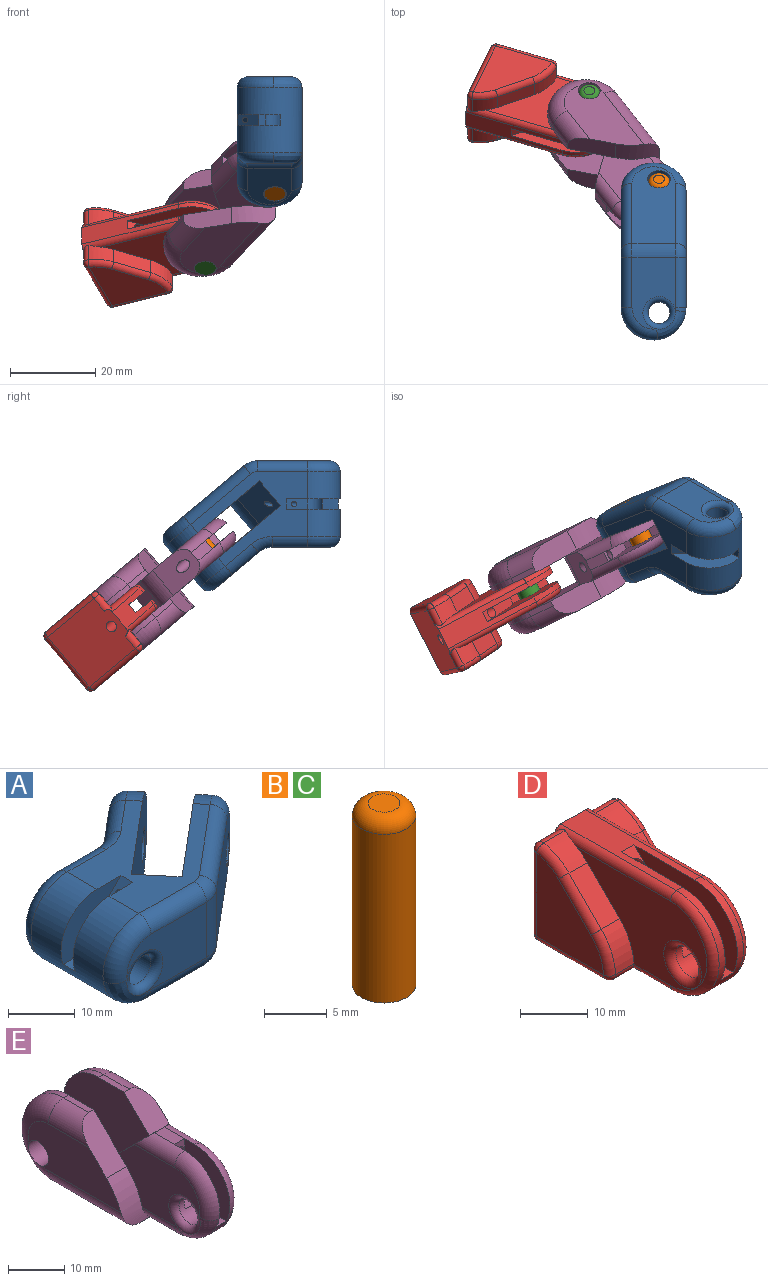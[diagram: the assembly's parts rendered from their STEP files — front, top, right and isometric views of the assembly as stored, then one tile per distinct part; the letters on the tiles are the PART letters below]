
ASSEMBLY  parts=5 mates=6
PART A: 47 faces, bbox 43.2x31.9x17 mm
  f0: cylinder r=7.62mm len=15.24mm, axis (0,1,0), area 327.8mm2, adj f9,f10,f21,f22,f23,f31,f32,f33
  f1: cylinder r=2.54mm len=17.78mm, axis (0,-1,0), area 266.9mm2, adj f17,f18,f41,f42,f43,f44
  f2: plane 20.43x17.14mm, normal (-0.64,0.77,0), area 264.5mm2, adj f3,f9,f10,f12,f13,f14,f15
  f3: plane 5.84x4.9mm, normal (0.77,0.64,0), area 24.3mm2, adj f2,f4,f10,f14
  f4: plane 20.43x17.14mm, normal (0.64,-0.77,0), area 264.5mm2, adj f3,f9,f10,f11,f13,f14,f16
  f5: plane 10.16x10.06mm, normal (-0.64,0.77,0), area 100mm2, adj f16,f19,f38,f39,f40
  f6: plane 13.39x10.16mm, normal (0,1,0), area 81.8mm2, adj f17,f19,f32,f33,f34,f35
  f7: plane 16.84x10.16mm, normal (0,-1,0), area 116.8mm2, adj f18,f20,f22,f23,f24,f25
  f8: plane 18.04x15.14mm, normal (0.64,-0.77,0), area 205.9mm2, adj f15,f20,f28,f29,f30
  f9: plane 27.54x22.2mm, normal (0,0,1), area 215.7mm2, adj f0,f2,f4,f11,f12,f13,f25,f27
  f10: plane 27.54x22.2mm, normal (0,0,-1), area 296.3mm2, adj f0,f2,f3,f4,f11,f12,f24,f26
  f11: cylinder r=7.62mm len=15.24mm, axis (0.64,-0.77,0), area 60.8mm2, adj f4,f9,f10,f40
  f12: cylinder r=7.62mm len=15.24mm, axis (0.64,-0.77,0), area 60.8mm2, adj f2,f9,f10,f30
  f13: plane 10.65x10.53mm, normal (0.54,0.45,0.71), area 69.4mm2, adj f2,f4,f9,f14,f45
  f14: cylinder r=7.62mm len=7.27mm, axis (-0.64,0.77,0), area 45.6mm2, adj f2,f3,f4,f13
  f15: cylinder r=2.67mm len=7.35mm, axis (0.64,-0.77,0), area 85.1mm2, adj f2,f8
  f16: cylinder r=2.67mm len=7.35mm, axis (0.64,-0.77,0), area 85.1mm2, adj f4,f5
  f17: torus R=3.81mm, axis (0,-1,0), area 37.6mm2, adj f1,f6,f31
  f18: torus R=3.81mm, axis (0,-1,0), area 37.6mm2, adj f1,f7,f21
  f19: cylinder r=5.08mm len=10.16mm, axis (0,0,-1), area 36mm2, adj f5,f6,f36,f37
  f20: cylinder r=5.08mm len=10.16mm, axis (0,0,-1), area 36mm2, adj f7,f8,f26,f27
  f21: bspline ~6.87x6.87mm, area 32.4mm2, adj f0,f18,f22,f23
  f22: torus R=5.08mm, axis (0,-1,0), area 3.6mm2, adj f0,f7,f21,f24
  f23: torus R=5.08mm, axis (0,-1,0), area 45.6mm2, adj f0,f7,f21,f25
  f24: cylinder r=2.54mm len=11.76mm, axis (1,0,0), area 46.9mm2, adj f7,f10,f22,f26
  f25: cylinder r=2.54mm len=11.76mm, axis (-1,0,0), area 46.9mm2, adj f7,f9,f23,f27
  f26: torus R=2.54mm, axis (0,0,1), area 11.6mm2, adj f10,f20,f24,f28
  f27: torus R=2.54mm, axis (0,0,1), area 11.6mm2, adj f9,f20,f25,f29
  f28: cylinder r=2.54mm len=15.78mm, axis (0.77,0.64,0), area 73.7mm2, adj f8,f10,f26,f30
  f29: cylinder r=2.54mm len=15.78mm, axis (-0.77,-0.64,0), area 73.7mm2, adj f8,f9,f27,f30
  f30: torus R=5.08mm, axis (0.64,-0.77,0), area 83.9mm2, adj f8,f12,f28,f29
  f31: bspline ~6.87x6.87mm, area 32.4mm2, adj f0,f17,f32,f33
  f32: torus R=5.08mm, axis (0,-1,0), area 45.6mm2, adj f0,f6,f31,f34
  f33: torus R=5.08mm, axis (0,-1,0), area 3.6mm2, adj f0,f6,f31,f35
  f34: cylinder r=2.54mm len=8.31mm, axis (1,0,0), area 33.2mm2, adj f6,f9,f32,f36
  f35: cylinder r=2.54mm len=8.31mm, axis (-1,0,0), area 33.2mm2, adj f6,f10,f33,f37
  f36: torus R=7.62mm, axis (0,0,1), area 16.7mm2, adj f9,f19,f34,f38
  f37: torus R=7.62mm, axis (0,0,1), area 16.7mm2, adj f10,f19,f35,f39
  f38: cylinder r=2.54mm len=7.8mm, axis (0.77,0.64,0), area 32.1mm2, adj f5,f9,f36,f40
  f39: cylinder r=2.54mm len=7.8mm, axis (-0.77,-0.64,0), area 32.1mm2, adj f5,f10,f37,f40
  f40: torus R=5.08mm, axis (-0.64,0.77,0), area 83.9mm2, adj f5,f11,f38,f39
  f41: plane 12.7x10.16mm, normal (0,1,0), area 64.6mm2, adj f0,f1,f9,f42,f44,f46
  f42: plane 2.54x1.61mm, normal (-1,0,0), area 4.1mm2, adj f1,f41,f43,f46
  f43: plane 12.7x10.16mm, normal (0,-1,0), area 64.6mm2, adj f0,f1,f9,f42,f44,f46
  f44: plane 3.71x2.54mm, normal (0,0,1), area 9.4mm2, adj f0,f1,f41,f43
  f45: cylinder r=0.64mm len=7.67mm, axis (-1,0,0), area 24.3mm2, adj f13,f46
  f46: plane 5.08x5.08mm, normal (-0.71,0,0.71), area 16.5mm2, adj f9,f41,f42,f43,f45
PART B: 4 faces, bbox 5.5x5.5x17.8 mm
  f0: cylinder r=2.54mm len=16.51mm, axis (0,0,-1), area 263.5mm2, adj f2,f3
  f1: plane 2.54x2.54mm, normal (0,0,1), area 5.1mm2, adj f3
  f2: plane 5.08x5.08mm, normal (0,0,-1), area 20.3mm2, adj f0
  f3: torus R=1.27mm, axis (0,0,1), area 26.1mm2, adj f0,f1
PART C: same geometry as B
PART D: 52 faces, bbox 17.8x33.8x19.2 mm
  f0: plane 7.62x7.62mm, normal (0,-0.71,0.71), area 23.8mm2, adj f10,f11,f14,f16
  f1: plane 24.13x5.08mm, normal (0,0,1), area 90.3mm2, adj f3,f7,f10,f11,f15,f23,f26
  f2: cylinder r=2.67mm len=5.33mm, axis (1,0,0), area 57.1mm2, adj f10,f11,f12,f13,f50,f51
  f3: cylinder r=8.89mm len=17.78mm, axis (-1,0,0), area 96.4mm2, adj f1,f9,f10,f11,f12,f24,f27
  f4: plane 27.22x15.24mm, normal (-1,0,0), area 226.5mm2, adj f18,f19,f22,f23,f24,f25,f49,f50
  f5: plane 27.22x15.24mm, normal (1,0,0), area 226.5mm2, adj f17,f20,f21,f26,f27,f28,f42,f51
  f6: plane 15.09x13.96mm, normal (1,0,0), area 138.1mm2, adj f33,f35,f38,f39,f40
  f7: plane 16.51x15.24mm, normal (0,1,0), area 235mm2, adj f1,f16,f23,f26,f29,f32,f35,f36
  f8: plane 15.09x13.96mm, normal (-1,0,0), area 138.1mm2, adj f29,f30,f45,f46,f47
  f9: plane 22.86x15.24mm, normal (0,0,-1), area 258mm2, adj f3,f25,f28,f30,f32,f33,f42,f49
  f10: plane 21.59x12.7mm, normal (-1,0,0), area 161.1mm2, adj f0,f1,f2,f3,f12,f13,f14,f15
  f11: plane 21.59x12.7mm, normal (1,0,0), area 161.1mm2, adj f0,f1,f2,f3,f12,f13,f14,f15
  f12: plane 3.15x2.54mm, normal (0,0,1), area 8mm2, adj f2,f3,f10,f11
  f13: plane 2.73x2.54mm, normal (0,0,1), area 6.9mm2, adj f2,f10,f11,f14
  f14: plane 2.54x2.54mm, normal (0,-1,0), area 6.5mm2, adj f0,f10,f11,f13
  f15: plane 2.54x2.54mm, normal (0,-0.71,0.71), area 5.5mm2, adj f1,f10,f11,f16
  f16: cylinder r=1.27mm len=15.24mm, axis (0,1,0), area 111.5mm2, adj f0,f7,f15
  f17: plane 6.76x6.76mm, normal (0,-0.71,0.71), area 36.4mm2, adj f5,f20,f21,f39
  f18: plane 6.76x6.76mm, normal (0,-0.71,0.71), area 36.4mm2, adj f4,f19,f22,f46
  f19: cylinder r=10.16mm len=6.73mm, axis (1,0,0), area 28.7mm2, adj f4,f18,f47,f49
  f20: cylinder r=10.16mm len=6.73mm, axis (1,0,0), area 28.7mm2, adj f5,f17,f40,f42
  f21: cylinder r=10.16mm len=5.27mm, axis (-1,0,0), area 23.8mm2, adj f5,f17,f26,f36,f38
  f22: cylinder r=10.16mm len=5.27mm, axis (-1,0,0), area 23.8mm2, adj f4,f18,f23,f43,f45
  f23: cylinder r=1.27mm len=24.13mm, axis (0,1,0), area 44.5mm2, adj f1,f4,f7,f22,f24,f43
  f24: torus R=7.62mm, axis (1,0,0), area 52.8mm2, adj f3,f4,f23,f25
  f25: cylinder r=1.27mm len=8.9mm, axis (0,-1,0), area 16.1mm2, adj f4,f9,f24,f49
  f26: cylinder r=1.27mm len=24.13mm, axis (0,-1,0), area 44.5mm2, adj f1,f5,f7,f21,f27,f36
  f27: torus R=7.62mm, axis (1,0,0), area 52.8mm2, adj f3,f5,f26,f28
  f28: cylinder r=1.27mm len=8.9mm, axis (0,1,0), area 16.1mm2, adj f5,f9,f27,f42
  f29: cylinder r=1.27mm len=15.09mm, axis (0,0,-1), area 30.1mm2, adj f7,f8,f31,f44
  f30: cylinder r=1.27mm len=13.96mm, axis (0,-1,0), area 27.9mm2, adj f8,f9,f31,f48
  f31: sphere r=1.27mm, area 2.5mm2, adj f29,f30,f32
  f32: cylinder r=1.27mm len=15.24mm, axis (-1,0,0), area 30.4mm2, adj f7,f9,f31,f34
  f33: cylinder r=1.27mm len=13.96mm, axis (0,1,0), area 27.9mm2, adj f6,f9,f34,f41
  f34: sphere r=1.27mm, area 2.5mm2, adj f32,f33,f35
  f35: cylinder r=1.27mm len=15.09mm, axis (0,0,1), area 30.1mm2, adj f6,f7,f34,f37
  f36: cylinder r=1.27mm len=4.48mm, axis (-1,0,0), area 9.2mm2, adj f7,f21,f26,f37
  f37: sphere r=1.27mm, area 2.8mm2, adj f35,f36,f38
  f38: torus R=8.89mm, axis (-1,0,0), area 11.5mm2, adj f6,f21,f37,f39
  f39: cylinder r=1.27mm len=7.65mm, axis (0,0.71,0.71), area 19.1mm2, adj f6,f17,f38,f40
  f40: torus R=8.89mm, axis (-1,0,0), area 14.3mm2, adj f6,f20,f39,f41
  f41: sphere r=1.27mm, area 2.6mm2, adj f33,f40,f42
  f42: cylinder r=1.27mm len=5.08mm, axis (1,0,0), area 8.7mm2, adj f5,f9,f20,f28,f41
  f43: cylinder r=1.27mm len=4.48mm, axis (-1,0,0), area 9.2mm2, adj f7,f22,f23,f44
  f44: sphere r=1.27mm, area 2.8mm2, adj f29,f43,f45
  f45: torus R=8.89mm, axis (-1,0,0), area 11.5mm2, adj f8,f22,f44,f46
  f46: cylinder r=1.27mm len=7.65mm, axis (0,0.71,0.71), area 19.1mm2, adj f8,f18,f45,f47
  f47: torus R=8.89mm, axis (-1,0,0), area 14.3mm2, adj f8,f19,f46,f48
  f48: sphere r=1.27mm, area 2.6mm2, adj f30,f47,f49
  f49: cylinder r=1.27mm len=5.08mm, axis (1,0,0), area 8.7mm2, adj f4,f9,f19,f25,f48
  f50: torus R=3.94mm, axis (1,0,0), area 39.2mm2, adj f2,f4
  f51: torus R=3.94mm, axis (1,0,0), area 39.2mm2, adj f2,f5
PART E: 48 faces, bbox 18.8x47x20.3 mm
  f0: plane 8.29x8.29mm, normal (0,-0.71,0.71), area 55.2mm2, adj f2,f3,f12,f13,f27,f32
  f1: plane 21.59x17.78mm, normal (-1,0,0), area 284.6mm2, adj f4,f11,f14,f15,f18,f25,f28,f29
  f2: plane 20.32x12.7mm, normal (-1,0,0), area 159.1mm2, adj f0,f27,f28,f30,f38,f39,f41,f42
  f3: plane 6.35x1.27mm, normal (0,0,1), area 8.1mm2, adj f0,f12,f16,f32
  f4: plane 6.35x1.27mm, normal (0,0,1), area 8.1mm2, adj f1,f15,f25,f35
  f5: plane 5.08x2.54mm, normal (0,0,1), area 12.9mm2, adj f22,f28,f38,f47
  f6: cylinder r=2.67mm len=5.33mm, axis (1,0,0), area 57.1mm2, adj f19,f20,f21,f24,f30,f31
  f7: cylinder r=8.89mm len=8.03mm, axis (-1,0,0), area 25.5mm2, adj f14,f19,f40,f41,f44,f45
  f8: cylinder r=1.27mm len=8.89mm, axis (0,1,0), area 60.5mm2, adj f22,f23,f28
  f9: plane 20.32x12.7mm, normal (1,0,0), area 159.1mm2, adj f25,f26,f28,f31,f43,f44,f46,f47
  f10: plane 23.31x10.16mm, normal (1,0,0), area 174.6mm2, adj f18,f25,f26,f35,f36,f37
  f11: plane 7.62x6.26mm, normal (0,1,0), area 47.7mm2, adj f1,f12,f14,f29
  f12: plane 21.59x17.78mm, normal (1,0,0), area 284.6mm2, adj f0,f3,f11,f14,f16,f17,f28,f29
  f13: plane 23.31x10.16mm, normal (-1,0,0), area 174.6mm2, adj f0,f17,f27,f32,f33,f34
  f14: plane 26.67x10.16mm, normal (0,0,-1), area 135.5mm2, adj f1,f7,f11,f12,f15,f16,f26,f27
  f15: cylinder r=8.89mm len=17.78mm, axis (1,0,0), area 35.5mm2, adj f1,f4,f14,f36
  f16: cylinder r=8.89mm len=17.78mm, axis (1,0,0), area 35.5mm2, adj f3,f12,f14,f33
  f17: cylinder r=2.54mm len=5.08mm, axis (1,0,0), area 80.9mm2, adj f12,f13,f33
  f18: cylinder r=2.54mm len=5.08mm, axis (1,0,0), area 80.9mm2, adj f1,f10,f36
  f19: plane 3.15x2.54mm, normal (0,0,1), area 8mm2, adj f6,f7,f21,f24
  f20: plane 2.73x2.54mm, normal (0,0,1), area 6.9mm2, adj f6,f21,f23,f24
  f21: plane 12.82x11.55mm, normal (-1,0,0), area 109.5mm2, adj f6,f19,f20,f22,f23,f45,f46,f47
  f22: plane 2.54x2.54mm, normal (0,-1,0), area 3.9mm2, adj f5,f8,f21,f24
  f23: plane 10.16x2.54mm, normal (0,-1,0), area 23.3mm2, adj f8,f20,f21,f24
  f24: plane 12.93x11.65mm, normal (1,0,0), area 109.5mm2, adj f6,f19,f20,f22,f23,f38,f39,f40
  f25: plane 8.29x8.29mm, normal (0,-0.71,0.71), area 55.2mm2, adj f1,f4,f9,f10,f26,f35
  f26: cylinder r=15.24mm len=9.49mm, axis (1,0,0), area 52.5mm2, adj f9,f10,f14,f25,f37,f43
  f27: cylinder r=15.24mm len=9.49mm, axis (1,0,0), area 52.5mm2, adj f0,f2,f13,f14,f34,f42
  f28: plane 8.69x8.1mm, normal (0,0.71,0.71), area 64.7mm2, adj f1,f2,f5,f8,f9,f12,f29,f38
  f29: cylinder r=6.35mm len=7.62mm, axis (-1,0,0), area 38mm2, adj f1,f11,f12,f28
  f30: torus R=3.94mm, axis (1,0,0), area 39.2mm2, adj f2,f6,f40
  f31: torus R=3.94mm, axis (1,0,0), area 39.2mm2, adj f6,f9,f45
  f32: cylinder r=3.81mm len=10.16mm, axis (0,1,0), area 46.3mm2, adj f0,f3,f13,f33
  f33: torus R=5.08mm, axis (-1,0,0), area 137.3mm2, adj f13,f16,f17,f32,f34
  f34: cylinder r=3.81mm len=19.05mm, axis (0,-1,0), area 111.5mm2, adj f13,f14,f27,f33
  f35: cylinder r=3.81mm len=10.16mm, axis (0,-1,0), area 46.3mm2, adj f4,f10,f25,f36
  f36: torus R=5.08mm, axis (-1,0,0), area 137.3mm2, adj f10,f15,f18,f35,f37
  f37: cylinder r=3.81mm len=19.05mm, axis (0,1,0), area 111.5mm2, adj f10,f14,f26,f36
  f38: cylinder r=2.54mm len=10.16mm, axis (0,1,0), area 35.5mm2, adj f2,f5,f24,f28,f39
  f39: torus R=6.35mm, axis (1,0,0), area 55.9mm2, adj f2,f24,f38,f40
  f40: bspline ~7.54x7.54mm, area 31.5mm2, adj f7,f24,f30,f39,f41
  f41: torus R=6.35mm, axis (1,0,0), area 6mm2, adj f2,f7,f40,f42
  f42: cylinder r=2.54mm len=8.05mm, axis (0,-1,0), area 31.3mm2, adj f2,f14,f27,f41
  f43: cylinder r=2.54mm len=8.05mm, axis (0,1,0), area 31.3mm2, adj f9,f14,f26,f44
  f44: torus R=6.35mm, axis (1,0,0), area 6mm2, adj f7,f9,f43,f45
  f45: bspline ~7.54x7.54mm, area 31.9mm2, adj f7,f21,f31,f44,f46
  f46: torus R=6.35mm, axis (1,0,0), area 55.9mm2, adj f9,f21,f45,f47
  f47: cylinder r=2.54mm len=10.16mm, axis (0,-1,0), area 35.5mm2, adj f5,f9,f21,f28,f46
PLACE A rot(axis=(-0.58,-0.58,0.58),120deg) t=(6.35,11.43,-10.16)mm
PLACE B rot(axis=(-0.69,0.25,0.68),55.8deg) t=(0,19.98,-17.34)mm
PLACE C rot(axis=(-0.14,-0.34,-0.93),138.8deg) t=(-16.36,40.83,-34.83)mm
PLACE D rot(axis=(0.24,-0.56,0.79),93.7deg) t=(-23.61,48.14,-40.96)mm
PLACE E rot(axis=(-0.08,-0.81,0.58),90.4deg) t=(0.21,29.16,-25.04)mm
MATE cylindrical C.f0 <-> E.f17  axis (0,-0.64,-0.77) through (-16.36,40.83,-34.83)mm
MATE cylindrical E.f6 <-> B.f0  axis (0,0.64,0.77) through (0,25.7,-10.53)mm
MATE cylindrical D.f50 <-> C.f0  axis (0,0.64,0.77) through (-16.36,44.91,-29.96)mm
MATE planar E.f2 <-> A.f4  axis (0,-0.64,-0.77) through (-6.58,26.39,-16.08)mm
MATE planar D.f5 <-> E.f1  axis (0,0.64,0.77) through (-24.51,47.95,-24.23)mm
MATE planar C.f0 <-> E.f10  axis (0,0.64,0.77) through (-16.36,52.26,-21.21)mm
